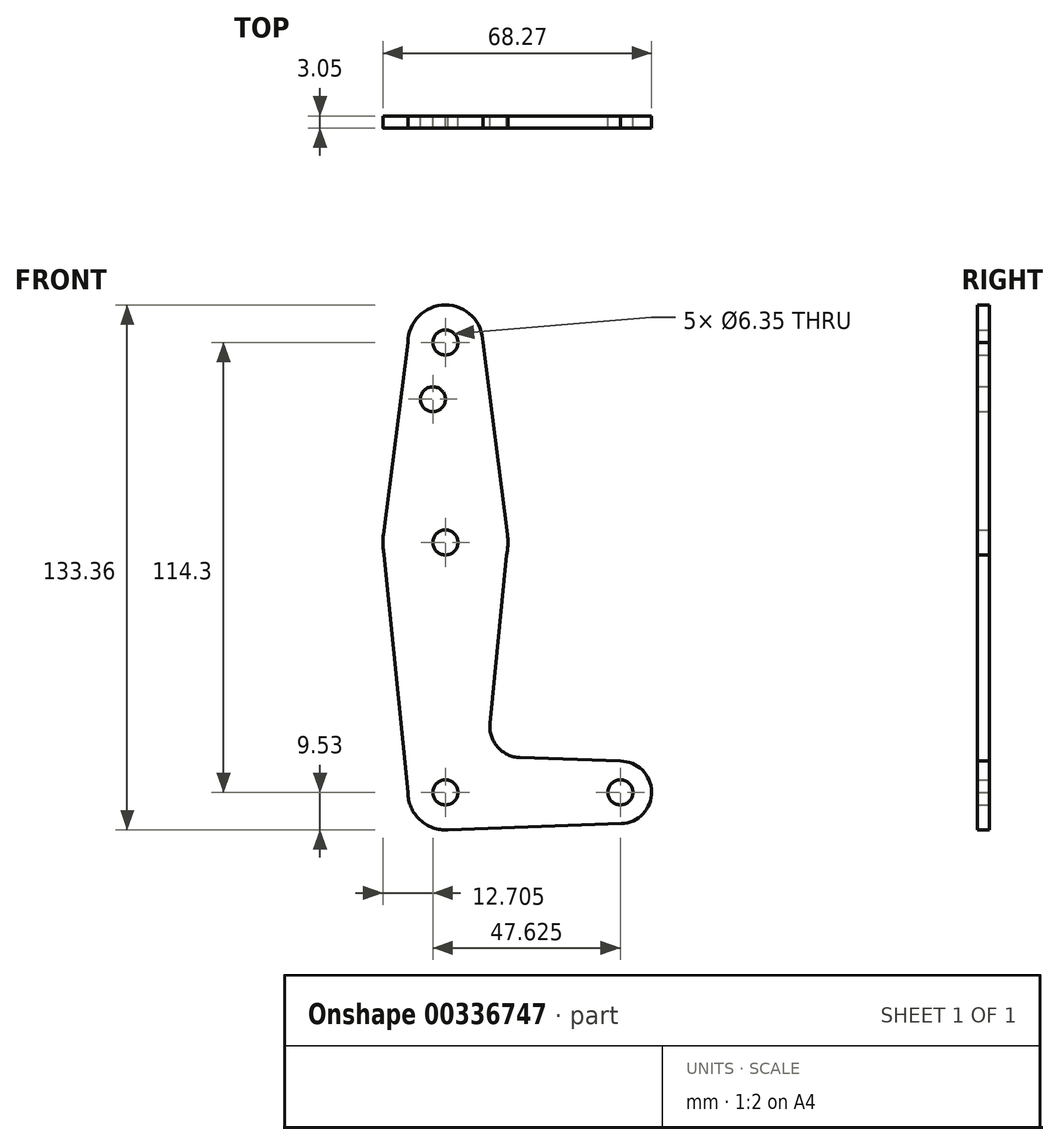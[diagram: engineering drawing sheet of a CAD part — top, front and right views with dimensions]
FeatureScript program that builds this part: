
annotation { "Feature Type Name" : "Feature", "Feature Type Description" : "" }
export const myFeature = defineFeature(function(context is Context, id is Id, definition is map)
    precondition{}
    {
        {
            var Q0;
            Q0=qCreatedBy(makeId("Front.planeOp"),FACE);
            var sketch = newSketch(context, id + "F0", { "sketchPlane" : qUnion([Q0])});
            skLineSegment(sketch, "E0", {"start": v(0, 0) * mm, "end": v(0, 114.3) * mm, "construction": true});
            skCircle(sketch, "E1", {"center": v(0, 114.3) * mm, "radius": 9.53 * mm});
            skCircle(sketch, "E2", {"center": v(0, 63.5) * mm, "radius": 15.88 * mm});
            skLineSegment(sketch, "E3", {"start": v(0, 0) * mm, "end": v(44.45, 0) * mm, "construction": true});
            skCircle(sketch, "E4", {"center": v(0, 0) * mm, "radius": 9.53 * mm});
            skCircle(sketch, "E5", {"center": v(44.45, 0) * mm, "radius": 7.94 * mm});
            skLineSegment(sketch, "E6", {"start": v(-9.53, 114.3) * mm, "end": v(-15.75, 65.5) * mm});
            skLineSegment(sketch, "E7", {"start": v(9.53, 114.3) * mm, "end": v(15.75, 65.5) * mm});
            skLineSegment(sketch, "E8", {"start": v(-15.56, 60.35) * mm, "end": v(-9.53, 0) * mm});
            skLineSegment(sketch, "E9", {"start": v(15.56, 60.35) * mm, "end": v(11.32, 17.58) * mm});
            skLineSegment(sketch, "E10", {"start": v(0, -9.53) * mm, "end": v(44.73, -7.93) * mm});
            skLineSegment(sketch, "E11", {"start": v(18.94, 8.85) * mm, "end": v(44.45, 7.94) * mm});
            skCircle(sketch, "E12", {"center": v(0, 114.3) * mm, "radius": 3.18 * mm});
            skCircle(sketch, "E13", {"center": v(-3.18, 99.89) * mm, "radius": 3.18 * mm});
            skCircle(sketch, "E14", {"center": v(0, 63.5) * mm, "radius": 3.18 * mm});
            skCircle(sketch, "E15", {"center": v(0, 0) * mm, "radius": 3.18 * mm});
            skCircle(sketch, "E16", {"center": v(44.45, 0) * mm, "radius": 3.18 * mm});
            skPoint(sketch, "E17.newPointB", {"position": v(9.57, 0) * mm});
            skArc(sketch, "E17.filletArc", {"start": v(11.32, 17.58) * mm, "mid": v(13.24, 11.56) * mm, "end": v(18.94, 8.85) * mm});
            skSolve(sketch);
        }
        {
            var Q0;
            Q0 = qSketchRegion(id + "F0", true);
            extrude(context, id + "F1", {"entities" : qUnion([Q0]), "depth" : 3.05 * mm});
        }
    });
